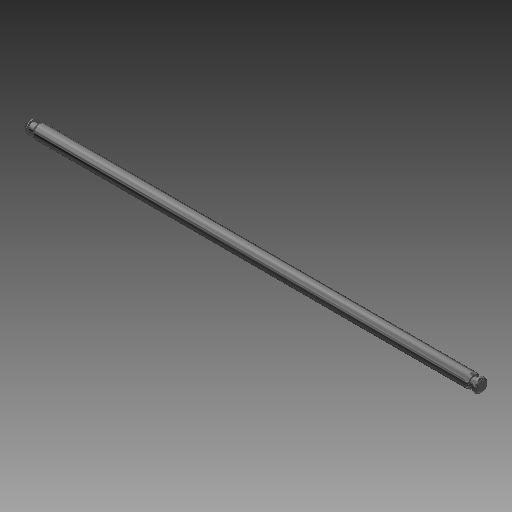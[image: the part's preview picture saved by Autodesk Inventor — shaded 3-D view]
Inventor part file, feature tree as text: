
AUTODESK INVENTOR PART (.ipt)
format: ipt  version: 2019 (Build 230136000, 136)  size: 126,976 bytes
history: native  units: mm
features: chamfer x2, revolve x1, fillet x1, plane x1, split x1, sketch x1
ambient origin geometry x8: Origin, YZ Plane, XZ Plane, XY Plane, X Axis, Y Axis, Z Axis, Center Point
bodies: Solid1 (feature_tree)
feature tree (7):
  revolve  "Revolution1"  [1 undecoded]
  chamfer  "Chamfer1"  Distance=12.0mm
  fillet  "Fillet1"  Radius=8.0mm
  chamfer  "Chamfer2"  Distance=12.0mm
  plane  "Work Plane1"
  split  "Split1"
  sketch  "Sketch1"  dims[d2=12.0mm d4=8.0mm d5=12.0mm d7=8.0mm d8=12.0mm d15=2.875mm d16=90.0deg d17=2.0mm d18=2.0mm d19=3.490659mm d20=0.5mm d21=2.95mm d22=4.5mm d23=2.95mm d24=4.5mm d25=2.0mm d26=2.0mm d27=3.490659mm d28=-114.5mm d29=387.0mm]
note: 1 required parameter value undecoded (feature->parameter linkage not recoverable at this tier; creation-order binding heuristic only, values carry confidence <= 0.55)
